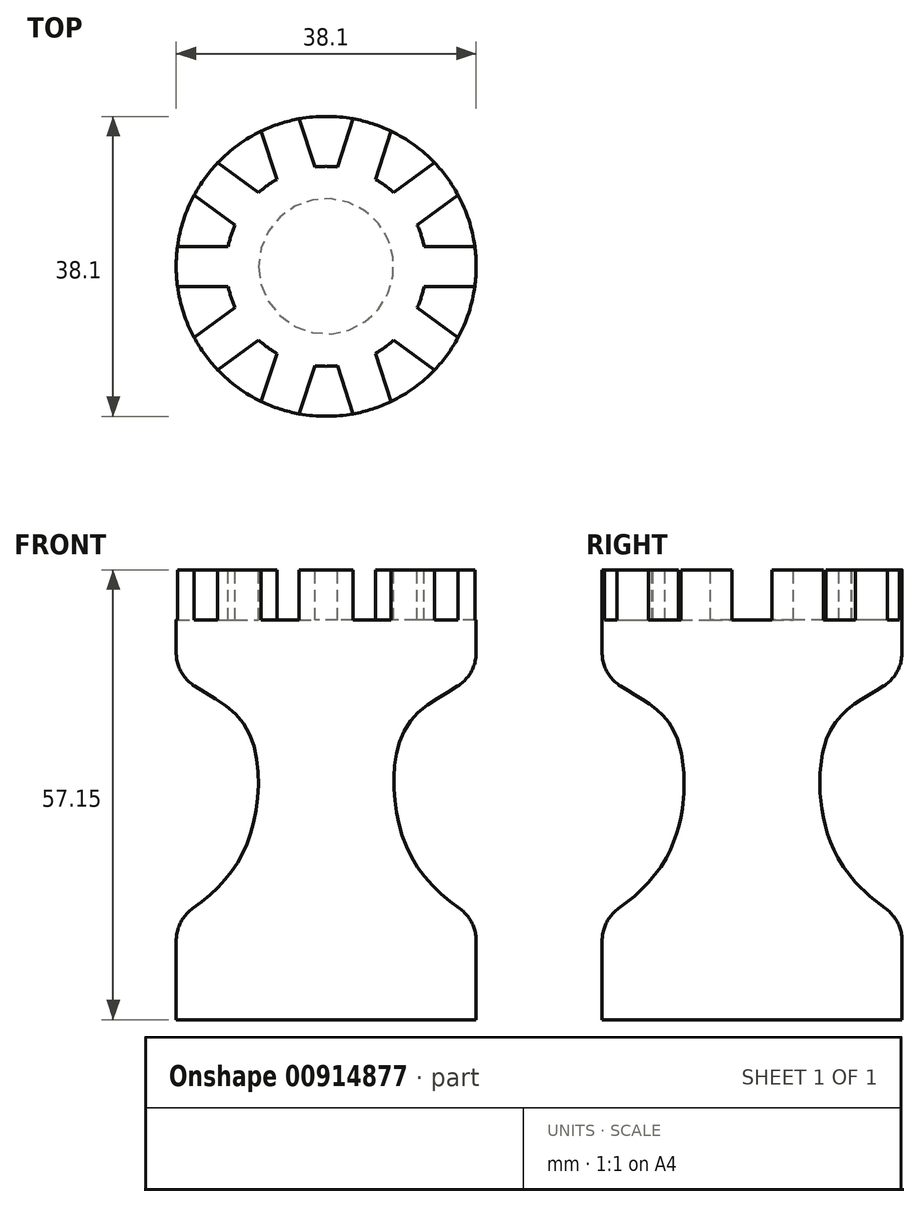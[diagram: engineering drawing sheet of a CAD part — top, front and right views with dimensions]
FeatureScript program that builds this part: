
annotation { "Feature Type Name" : "Feature", "Feature Type Description" : "" }
export const myFeature = defineFeature(function(context is Context, id is Id, definition is map)
    precondition{}
    {
        {
            var Q0;
            Q0=qCreatedBy(makeId("Front.planeOp"),FACE);
            var sketch = newSketch(context, id + "F0", { "sketchPlane" : qUnion([Q0])});
            skLineSegment(sketch, "E0", {"start": v(0, 0) * mm, "end": v(0, 57.15) * mm});
            skLineSegment(sketch, "E1", {"start": v(0, 0) * mm, "end": v(19.05, 0) * mm});
            skLineSegment(sketch, "E2", {"start": v(19.05, 0) * mm, "end": v(19.05, 12.7) * mm});
            skLineSegment(sketch, "E3", {"start": v(0, 44.45) * mm, "end": v(35.48, 44.45) * mm, "construction": true});
            skFitSpline(sketch, "E4", {"points": [v(19.05, 12.7) * mm, v(12.2, 18.57) * mm, v(8.85, 26.91) * mm, v(11.04, 38.36) * mm, v(19.05, 44.45) * mm], "startDerivative": vector(-34.51, 22.13) * mm, "endDerivative": vector(16.58, 26.51) * mm});
            skLineSegment(sketch, "E5.bottom", {"start": v(0, 44.45) * mm, "end": v(19.05, 44.45) * mm});
            skLineSegment(sketch, "E5.top", {"start": v(0, 57.15) * mm, "end": v(19.05, 57.15) * mm});
            skLineSegment(sketch, "E5.left", {"start": v(0, 44.45) * mm, "end": v(0, 57.15) * mm});
            skLineSegment(sketch, "E5.right", {"start": v(19.05, 44.45) * mm, "end": v(19.05, 57.15) * mm});
            skSolve(sketch);
        }
        {
            var Q0;
            {var subQ2=sQuery(id+"F0.wireOp",EDGE,"E5.bottom");Q0=makeQuery(id+"F0.imprint","IMPRINT",FACE,{"disambiguationData":[TD([[makeQuery(id+"F0.imprint","IMPRINT",EDGE,{"derivedFrom":subQ2}),1.0]])]});}
            var Q1;
            {var subQ0=sQuery(id+"F0.wireOp",EDGE,"E1");Q1=makeQuery(id+"F0.imprint","IMPRINT",FACE,{"disambiguationData":[TD([[makeQuery(id+"F0.imprint","IMPRINT",EDGE,{"derivedFrom":subQ0}),1.0]])]});}
            var Q2;
            Q2=sQuery(id+"F0.wireOp",EDGE,"E0");
            revolve(context, id + "F1", {"surfaceOperationType" : NewSurfaceOperationType.NEW, "entities" : qUnion([Q0, Q1]), "axis" : qUnion([Q2]), "revolveType" : RevolveType.FULL});
        }
        {
            var Q0;
            Q0=makeQuery(id+"F1.opRevolve","SWEPT_FACE",FACE,{"disambiguationData":[OSD([sQuery(id+"F0.wireOp",EDGE,"E5.top")])]});
            var sketch = newSketch(context, id + "F2", { "sketchPlane" : qUnion([Q0])});
            skCircle(sketch, "E6", {"center": v(0, 0) * mm, "radius": 12.7 * mm});
            skSolve(sketch);
        }
        {
            var Q0;
            Q0=makeQuery(id+"F2.imprint","IMPRINT",FACE,{"disambiguationData":[TD([[makeQuery(id+"F2.imprint","IMPRINT",EDGE,{"derivedFrom":sQuery(id+"F2.wireOp",EDGE,"E6")}),1.0]])]});
            extrude(context, id + "F3", {"entities" : qUnion([Q0]), "operationType" : NewBodyOperationType.REMOVE, "oppositeDirection" : true, "depth" : 6.35 * mm, "offsetDistance" : 25.4 * mm});
        }
        {
            var Q0;
            Q0=makeQuery(id+"F1.opRevolve","SWEPT_FACE",FACE,{"disambiguationData":[OSD([sQuery(id+"F0.wireOp",EDGE,"E5.top")])]});
            var sketch = newSketch(context, id + "F4", { "sketchPlane" : qUnion([Q0])});
            skLineSegment(sketch, "E7", {"start": v(0, 0) * mm, "end": v(19.05, 0) * mm, "construction": true});
            skLineSegment(sketch, "E8.bottom", {"start": v(26.22, -2.54) * mm, "end": v(11.88, -2.54) * mm});
            skLineSegment(sketch, "E8.top", {"start": v(26.22, 2.54) * mm, "end": v(11.88, 2.54) * mm});
            skLineSegment(sketch, "E8.left", {"start": v(26.22, -2.54) * mm, "end": v(26.22, 2.54) * mm});
            skLineSegment(sketch, "E8.right", {"start": v(11.88, -2.54) * mm, "end": v(11.88, 2.54) * mm});
            skPoint(sketch, "E8.middle", {"position": v(19.05, 0) * mm});
            skLineSegment(sketch, "E9.1.0", {"start": v(22.7, 13.36) * mm, "end": v(19.72, 17.47) * mm});
            skLineSegment(sketch, "E9.1.1", {"start": v(19.72, 17.47) * mm, "end": v(8.11, 9.04) * mm});
            skLineSegment(sketch, "E9.1.2", {"start": v(22.7, 13.36) * mm, "end": v(11.1, 4.93) * mm});
            skLineSegment(sketch, "E9.1.3", {"start": v(11.1, 4.93) * mm, "end": v(8.11, 9.04) * mm});
            skPoint(sketch, "E9.1.4", {"position": v(15.41, 11.2) * mm});
            skLineSegment(sketch, "E9.2.0", {"start": v(10.52, 24.16) * mm, "end": v(5.69, 25.73) * mm});
            skLineSegment(sketch, "E9.2.1", {"start": v(5.69, 25.73) * mm, "end": v(1.25, 12.08) * mm});
            skLineSegment(sketch, "E9.2.2", {"start": v(10.52, 24.16) * mm, "end": v(6.09, 10.5) * mm});
            skLineSegment(sketch, "E9.2.3", {"start": v(6.09, 10.5) * mm, "end": v(1.25, 12.08) * mm});
            skPoint(sketch, "E9.2.4", {"position": v(5.89, 18.12) * mm});
            skLineSegment(sketch, "E9.3.0", {"start": v(-5.69, 25.73) * mm, "end": v(-10.52, 24.16) * mm});
            skLineSegment(sketch, "E9.3.1", {"start": v(-10.52, 24.16) * mm, "end": v(-6.09, 10.5) * mm});
            skLineSegment(sketch, "E9.3.2", {"start": v(-5.69, 25.73) * mm, "end": v(-1.25, 12.08) * mm});
            skLineSegment(sketch, "E9.3.3", {"start": v(-1.25, 12.08) * mm, "end": v(-6.09, 10.5) * mm});
            skPoint(sketch, "E9.3.4", {"position": v(-5.89, 18.12) * mm});
            skLineSegment(sketch, "E9.4.0", {"start": v(-19.72, 17.47) * mm, "end": v(-22.7, 13.36) * mm});
            skLineSegment(sketch, "E9.4.1", {"start": v(-22.7, 13.36) * mm, "end": v(-11.1, 4.93) * mm});
            skLineSegment(sketch, "E9.4.2", {"start": v(-19.72, 17.47) * mm, "end": v(-8.12, 9.04) * mm});
            skLineSegment(sketch, "E9.4.3", {"start": v(-8.12, 9.04) * mm, "end": v(-11.1, 4.93) * mm});
            skPoint(sketch, "E9.4.4", {"position": v(-15.41, 11.2) * mm});
            skLineSegment(sketch, "E9.5.0", {"start": v(-26.22, 2.54) * mm, "end": v(-26.22, -2.54) * mm});
            skLineSegment(sketch, "E9.5.1", {"start": v(-26.22, -2.54) * mm, "end": v(-11.88, -2.54) * mm});
            skLineSegment(sketch, "E9.5.2", {"start": v(-26.22, 2.54) * mm, "end": v(-11.88, 2.54) * mm});
            skLineSegment(sketch, "E9.5.3", {"start": v(-11.88, 2.54) * mm, "end": v(-11.88, -2.54) * mm});
            skPoint(sketch, "E9.5.4", {"position": v(-19.05, 0) * mm});
            skLineSegment(sketch, "E9.6.0", {"start": v(-22.7, -13.36) * mm, "end": v(-19.72, -17.47) * mm});
            skLineSegment(sketch, "E9.6.1", {"start": v(-19.72, -17.47) * mm, "end": v(-8.12, -9.04) * mm});
            skLineSegment(sketch, "E9.6.2", {"start": v(-22.7, -13.36) * mm, "end": v(-11.1, -4.93) * mm});
            skLineSegment(sketch, "E9.6.3", {"start": v(-11.1, -4.93) * mm, "end": v(-8.12, -9.04) * mm});
            skPoint(sketch, "E9.6.4", {"position": v(-15.41, -11.2) * mm});
            skLineSegment(sketch, "E9.7.0", {"start": v(-10.52, -24.16) * mm, "end": v(-5.69, -25.73) * mm});
            skLineSegment(sketch, "E9.7.1", {"start": v(-5.69, -25.73) * mm, "end": v(-1.25, -12.08) * mm});
            skLineSegment(sketch, "E9.7.2", {"start": v(-10.52, -24.16) * mm, "end": v(-6.09, -10.5) * mm});
            skLineSegment(sketch, "E9.7.3", {"start": v(-6.09, -10.5) * mm, "end": v(-1.25, -12.08) * mm});
            skPoint(sketch, "E9.7.4", {"position": v(-5.89, -18.12) * mm});
            skLineSegment(sketch, "E9.8.0", {"start": v(5.69, -25.73) * mm, "end": v(10.52, -24.16) * mm});
            skLineSegment(sketch, "E9.8.1", {"start": v(10.52, -24.16) * mm, "end": v(6.09, -10.5) * mm});
            skLineSegment(sketch, "E9.8.2", {"start": v(5.69, -25.73) * mm, "end": v(1.25, -12.08) * mm});
            skLineSegment(sketch, "E9.8.3", {"start": v(1.25, -12.08) * mm, "end": v(6.09, -10.5) * mm});
            skPoint(sketch, "E9.8.4", {"position": v(5.89, -18.12) * mm});
            skLineSegment(sketch, "E9.9.0", {"start": v(19.72, -17.47) * mm, "end": v(22.7, -13.36) * mm});
            skLineSegment(sketch, "E9.9.1", {"start": v(22.7, -13.36) * mm, "end": v(11.1, -4.93) * mm});
            skLineSegment(sketch, "E9.9.2", {"start": v(19.72, -17.47) * mm, "end": v(8.11, -9.04) * mm});
            skLineSegment(sketch, "E9.9.3", {"start": v(8.11, -9.04) * mm, "end": v(11.1, -4.93) * mm});
            skPoint(sketch, "E9.9.4", {"position": v(15.41, -11.2) * mm});
            skPoint(sketch, "E9.center", {"position": v(0, 0) * mm});
            skSolve(sketch);
        }
        {
            var Q0;
            Q0 = qSketchRegion(id + "F4", true);
            extrude(context, id + "F5", {"entities" : qUnion([Q0]), "operationType" : NewBodyOperationType.REMOVE, "oppositeDirection" : true, "depth" : 6.35 * mm, "offsetDistance" : 25.4 * mm});
        }
        {
            var Q0;
            Q0=makeQuery(id+"F1.opRevolve","SWEPT_EDGE",EDGE,{"disambiguationData":[OSD([sQuery(id+"F0.wireOp",EDGE,"E2"),sQuery(id+"F0.wireOp",EDGE,"E4")])]});
            var Q1;
            Q1=makeQuery(id+"F1.opRevolve","SWEPT_EDGE",EDGE,{"disambiguationData":[OSD([sQuery(id+"F0.wireOp",EDGE,"E4"),sQuery(id+"F0.wireOp",EDGE,"E5.bottom"),sQuery(id+"F0.wireOp",EDGE,"E5.right")])]});
            fillet(context, id + "F6", {"entities" : qUnion([Q0, Q1]), "radius" : 5.08 * mm, "tangentPropagation" : true, "allowEdgeOverflow" : false});
        }
    });
